# Revit family: DL POWER LED MINI
name_source: partatom
category: Осветительные приборы
revit_build: Autodesk Revit 2016 (Build: 20150220_1215(x64)
units: mm (PartAtom-declared; Revit-internal decimal feet)

## family parameters
Источник света = Да
Общий = Нет
Основа = Грань
При загрузке вырезать с полостями = Нет
Размер круглого соединителя = Использовать диаметр
Тип детали = Нормальный
Точка расчета площади = Нет

## types (1)
- DL POWER LED MINI
    ADSK_Единица измерения = Шт.
    ADSK_Завод-изготовитель = ООО МГК Световые технологии
    ADSK_Количество фаз = 1
    ADSK_Количество фаз числовое = 1
    ADSK_Коэффициент мощности = 0.95
    ADSK_Масса = 0.9
    ADSK_Наименование = Компактный светодиодный светильник в корпусе из литого под давлением алюминия. Световая отдача прибора достигает 100 лм/Вт, существует возможность выбора углов рефлектора для создания различных сцен освещения. Светильник имеет широкие возможности по монтажу
    ADSK_Напряжение = 230 В
    ADSK_Номинальная мощность = 0 кВт
    ADSK_Полная мощность = 0 кВ·А
    ADSK_Размер_Высота = 90 мм
    ADSK_Размер_Ширина = 154 мм
    ADSK_Ток = 0 А
    ADSK_Энергоэффективность = 0 лм/Вт
    IP Class = IP20
    URL = https://ltcompany.com
    Блок аварийного питания = Нет
    Видимая форма излучения при визуализации = Нет
    Группа модели = Светильники
    Изготовитель = ООО МГК Световые технологии
    Излучение по длине прямоугольника = 154 мм
    Излучение по ширине прямоугольника = 154 мм
    Класс Защиты = II
    Климатическая зона = УХЛ4
    Код по классификатору = D5020200
    Корпус = Белый металл
    Область использования = Гипер-/супермаркеты, Конференц-залы, Культурно-развлекательные учреждения, Лестницы/коридоры, Магазины/бутики, Офисно-административные объекты, ТРЦ
    Описание = Компактный светодиодный светильник в корпусе из литого под давлением алюминия. Световая отдача прибора достигает 100 лм/Вт, существует возможность выбора углов рефлектора для создания различных сцен освещения. Светильник имеет широкие возможности по монтажу
    Отметка по умолчанию = 0 мм
    Плафон = Плафон самосвечение
    Полная установленная мощность = 0 кВ·А
    Разработчик = ООО ПРОРУБИМ
    Разработчик (телефон) = +7 (495) 649-85-43
    Светофильтр = 16777215
    Смещение цветовой температуры при затухании лампы = <Нет>
    Теплообменник = Черный металл
    Тип ИС = LED
    Тип ПРА = Драйвер
    Тип продукции = Светильник
    Угол наклона = -90.00°
    Файл фотометрической сетки = generic
